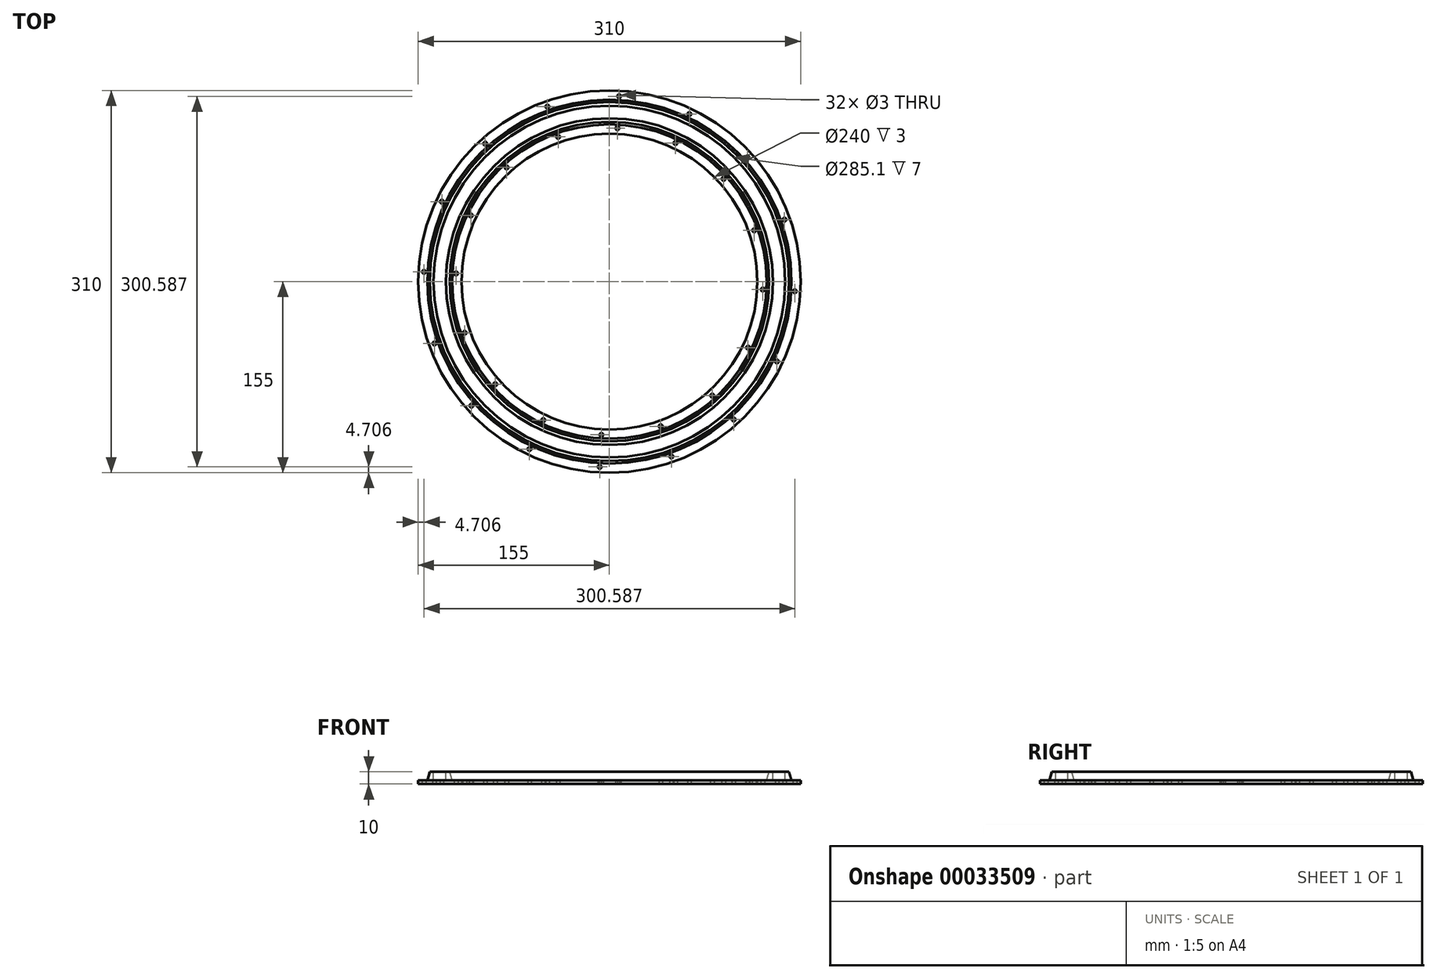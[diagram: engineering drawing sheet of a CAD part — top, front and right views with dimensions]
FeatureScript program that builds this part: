
annotation { "Feature Type Name" : "Feature", "Feature Type Description" : "" }
export const myFeature = defineFeature(function(context is Context, id is Id, definition is map)
    precondition{}
    {
        {
            var Q0;
            Q0=qCreatedBy(makeId("Top.planeOp"),FACE);
            var sketch = newSketch(context, id + "F0", { "sketchPlane" : qUnion([Q0])});
            skCircle(sketch, "E0", {"center": v(0, 0) * mm, "radius": 120 * mm});
            skCircle(sketch, "E1", {"center": v(0, 0) * mm, "radius": 155 * mm});
            skLineSegment(sketch, "E2", {"start": v(0, 0) * mm, "end": v(-155, 0) * mm, "construction": true});
            skLineSegment(sketch, "E3", {"start": v(0, 0) * mm, "end": v(-154.79, 8.11) * mm, "construction": true});
            skCircle(sketch, "E4", {"center": v(-150.3, 7.88) * mm, "radius": 1.5 * mm});
            skCircle(sketch, "E5", {"center": v(-124.33, 6.52) * mm, "radius": 1.5 * mm});
            skCircle(sketch, "E6.1.0", {"center": v(-141.87, -50.24) * mm, "radius": 1.5 * mm});
            skCircle(sketch, "E6.1.1", {"center": v(-117.36, -41.56) * mm, "radius": 1.5 * mm});
            skCircle(sketch, "E6.2.0", {"center": v(-111.84, -100.7) * mm, "radius": 1.5 * mm});
            skCircle(sketch, "E6.2.1", {"center": v(-92.52, -83.3) * mm, "radius": 1.5 * mm});
            skCircle(sketch, "E6.3.0", {"center": v(-64.8, -135.84) * mm, "radius": 1.5 * mm});
            skCircle(sketch, "E6.3.1", {"center": v(-53.6, -112.37) * mm, "radius": 1.5 * mm});
            skCircle(sketch, "E6.4.0", {"center": v(-7.88, -150.3) * mm, "radius": 1.5 * mm});
            skCircle(sketch, "E6.4.1", {"center": v(-6.52, -124.33) * mm, "radius": 1.5 * mm});
            skCircle(sketch, "E6.5.0", {"center": v(50.24, -141.87) * mm, "radius": 1.5 * mm});
            skCircle(sketch, "E6.5.1", {"center": v(41.56, -117.36) * mm, "radius": 1.5 * mm});
            skCircle(sketch, "E6.6.0", {"center": v(100.7, -111.84) * mm, "radius": 1.5 * mm});
            skCircle(sketch, "E6.6.1", {"center": v(83.3, -92.52) * mm, "radius": 1.5 * mm});
            skCircle(sketch, "E6.7.0", {"center": v(135.84, -64.8) * mm, "radius": 1.5 * mm});
            skCircle(sketch, "E6.7.1", {"center": v(112.37, -53.6) * mm, "radius": 1.5 * mm});
            skCircle(sketch, "E6.8.0", {"center": v(150.3, -7.88) * mm, "radius": 1.5 * mm});
            skCircle(sketch, "E6.8.1", {"center": v(124.33, -6.52) * mm, "radius": 1.5 * mm});
            skCircle(sketch, "E6.9.0", {"center": v(141.87, 50.24) * mm, "radius": 1.5 * mm});
            skCircle(sketch, "E6.9.1", {"center": v(117.36, 41.56) * mm, "radius": 1.5 * mm});
            skCircle(sketch, "E6.10.0", {"center": v(111.84, 100.7) * mm, "radius": 1.5 * mm});
            skCircle(sketch, "E6.10.1", {"center": v(92.52, 83.3) * mm, "radius": 1.5 * mm});
            skCircle(sketch, "E6.11.0", {"center": v(64.8, 135.84) * mm, "radius": 1.5 * mm});
            skCircle(sketch, "E6.11.1", {"center": v(53.6, 112.37) * mm, "radius": 1.5 * mm});
            skCircle(sketch, "E6.12.0", {"center": v(7.88, 150.3) * mm, "radius": 1.5 * mm});
            skCircle(sketch, "E6.12.1", {"center": v(6.52, 124.33) * mm, "radius": 1.5 * mm});
            skCircle(sketch, "E6.13.0", {"center": v(-50.24, 141.87) * mm, "radius": 1.5 * mm});
            skCircle(sketch, "E6.13.1", {"center": v(-41.56, 117.36) * mm, "radius": 1.5 * mm});
            skCircle(sketch, "E6.14.0", {"center": v(-100.7, 111.84) * mm, "radius": 1.5 * mm});
            skCircle(sketch, "E6.14.1", {"center": v(-83.3, 92.52) * mm, "radius": 1.5 * mm});
            skCircle(sketch, "E6.15.0", {"center": v(-135.84, 64.8) * mm, "radius": 1.5 * mm});
            skCircle(sketch, "E6.15.1", {"center": v(-112.37, 53.6) * mm, "radius": 1.5 * mm});
            skSolve(sketch);
        }
        {
            var Q0;
            Q0=makeQuery(id+"F0.imprint","IMPRINT",FACE,{"disambiguationData":[TD([[makeQuery(id+"F0.imprint","IMPRINT",EDGE,{"derivedFrom":sQuery(id+"F0.wireOp",EDGE,"E0")}),-1.0]])]});
            extrude(context, id + "F1", {"entities" : qUnion([Q0]), "depth" : 10 * mm});
        }
        {
            var Q0;
            Q0=qCreatedBy(makeId("Front.planeOp"),FACE);
            var sketch = newSketch(context, id + "F2", { "sketchPlane" : qUnion([Q0])});
            skLineSegment(sketch, "E7.bottom", {"start": v(-155, 0) * mm, "end": v(-120, 0) * mm, "construction": true});
            skLineSegment(sketch, "E7.top", {"start": v(-155, 10) * mm, "end": v(-120, 10) * mm, "construction": true});
            skLineSegment(sketch, "E7.left", {"start": v(-155, 0) * mm, "end": v(-155, 10) * mm, "construction": true});
            skLineSegment(sketch, "E7.right", {"start": v(-120, 0) * mm, "end": v(-120, 10) * mm, "construction": true});
            skLineSegment(sketch, "E8", {"start": v(-155, 3) * mm, "end": v(-147.55, 3) * mm});
            skLineSegment(sketch, "E9", {"start": v(-147.55, 3) * mm, "end": v(-145.55, 10) * mm});
            skLineSegment(sketch, "E10", {"start": v(-145.55, 10) * mm, "end": v(-142.55, 10) * mm});
            skLineSegment(sketch, "E11", {"start": v(-142.55, 10) * mm, "end": v(-142.55, 3) * mm});
            skLineSegment(sketch, "E12", {"start": v(-142.55, 3) * mm, "end": v(-132.45, 3) * mm});
            skLineSegment(sketch, "E13", {"start": v(-132.45, 3) * mm, "end": v(-132.45, 10) * mm});
            skLineSegment(sketch, "E14", {"start": v(-132.45, 10) * mm, "end": v(-129.45, 10) * mm});
            skLineSegment(sketch, "E15", {"start": v(-129.45, 10) * mm, "end": v(-127.45, 3) * mm});
            skLineSegment(sketch, "E16", {"start": v(-127.45, 3) * mm, "end": v(-120, 3) * mm});
            skLineSegment(sketch, "E17", {"start": v(-155, 3) * mm, "end": v(-155, 10) * mm});
            skLineSegment(sketch, "E18", {"start": v(-142.55, 10) * mm, "end": v(-132.45, 10) * mm});
            skLineSegment(sketch, "E19", {"start": v(-155, 10) * mm, "end": v(-155, 3) * mm});
            skLineSegment(sketch, "E20", {"start": v(-147.55, 3) * mm, "end": v(-155, 3) * mm});
            skLineSegment(sketch, "E21", {"start": v(-145.55, 10) * mm, "end": v(-155, 10) * mm});
            skLineSegment(sketch, "E22", {"start": v(-129.45, 10) * mm, "end": v(-120, 10) * mm});
            skLineSegment(sketch, "E23", {"start": v(-120, 10) * mm, "end": v(-120, 3) * mm});
            skLineSegment(sketch, "E24", {"start": v(0, 0) * mm, "end": v(0, 96.8) * mm, "construction": true});
            skSolve(sketch);
        }
        {
            var Q0;
            Q0 = qSketchRegion(id + "F2", true);
            var Q1;
            Q1=sQuery(id+"F2.wireOp",EDGE,"E24");
            revolve(context, id + "F3", {"operationType" : NewBodyOperationType.REMOVE, "entities" : qUnion([Q0]), "axis" : qUnion([Q1]), "revolveType" : RevolveType.FULL, "oppositeDirection" : true});
        }
    });
